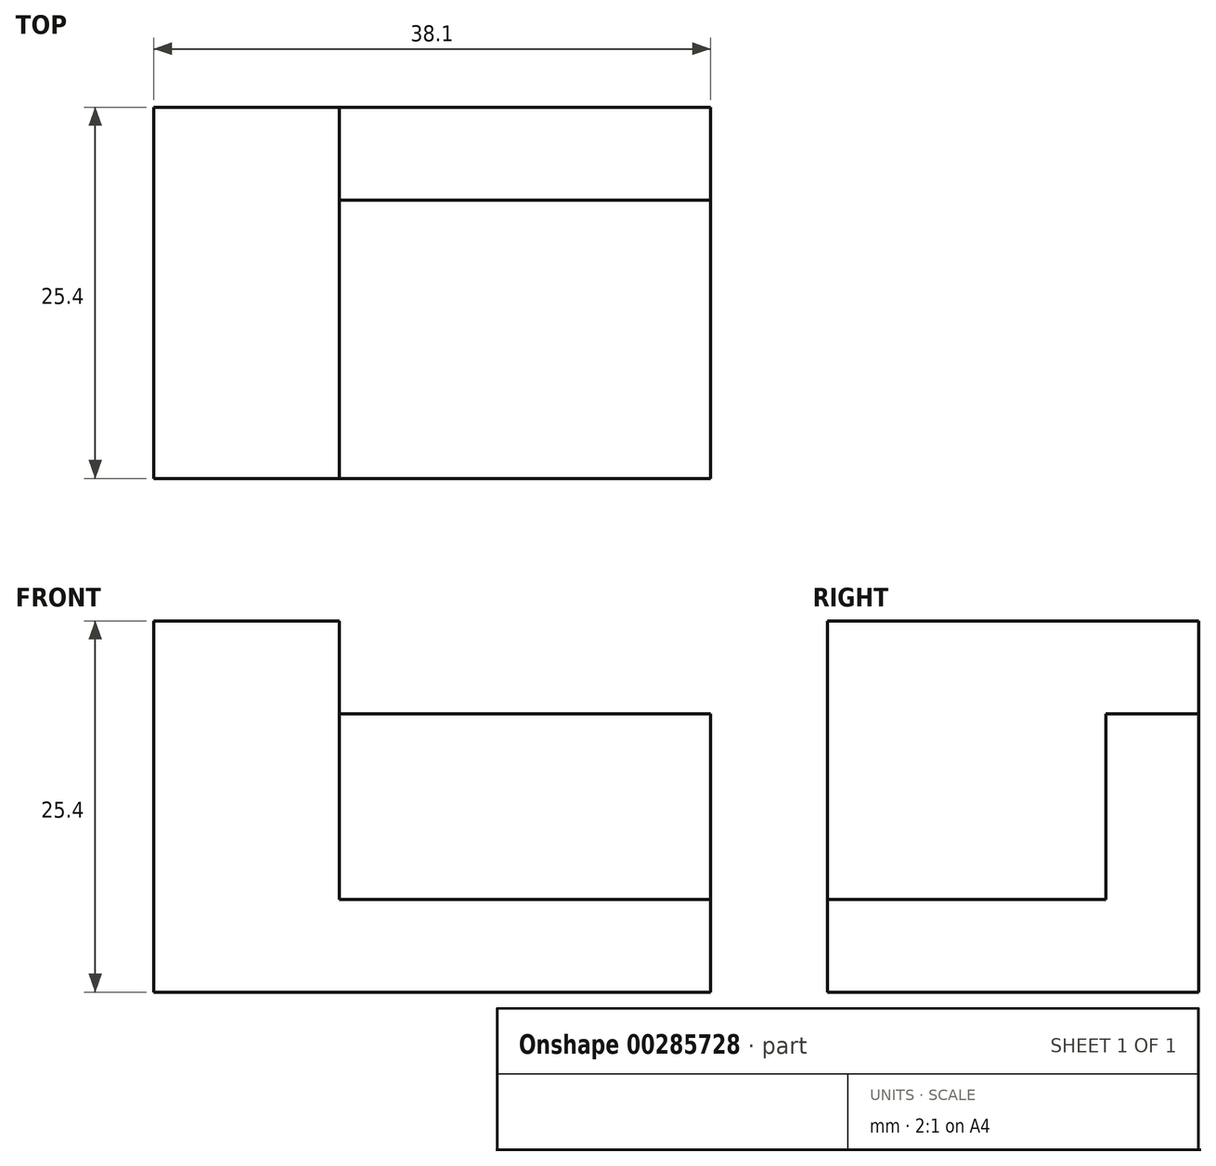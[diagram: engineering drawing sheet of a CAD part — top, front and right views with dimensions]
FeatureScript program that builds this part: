
annotation { "Feature Type Name" : "Feature", "Feature Type Description" : "" }
export const myFeature = defineFeature(function(context is Context, id is Id, definition is map)
    precondition{}
    {
        {
            var Q0;
            Q0=qCreatedBy(makeId("Right.planeOp"),FACE);
            var sketch = newSketch(context, id + "F0", { "sketchPlane" : qUnion([Q0])});
            skLineSegment(sketch, "E0.bottom", {"start": v(0, 25.4) * mm, "end": v(25.4, 25.4) * mm});
            skLineSegment(sketch, "E0.top", {"start": v(0, 0) * mm, "end": v(25.4, 0) * mm});
            skLineSegment(sketch, "E0.left", {"start": v(0, 25.4) * mm, "end": v(0, 0) * mm});
            skLineSegment(sketch, "E0.right", {"start": v(25.4, 25.4) * mm, "end": v(25.4, 0) * mm});
            skSolve(sketch);
        }
        {
            var Q0;
            Q0=makeQuery(id+"F0.imprint","IMPRINT",FACE,{"disambiguationData":[TD([[makeQuery(id+"F0.imprint","IMPRINT",EDGE,{"derivedFrom":sQuery(id+"F0.wireOp",EDGE,"E0.bottom")}),-1.0]])]});
            extrude(context, id + "F1", {"entities" : qUnion([Q0]), "depth" : 38.1 * mm});
        }
        {
            var Q0;
            Q0=makeQuery(id+"F1.opExtrude","CAP_FACE",FACE,{"disambiguationData":[OSD([sQuery(id+"F0.wireOp",EDGE,"E0.bottom"),sQuery(id+"F0.wireOp",EDGE,"E0.top"),sQuery(id+"F0.wireOp",EDGE,"E0.left"),sQuery(id+"F0.wireOp",EDGE,"E0.right")])],"isStart":false});
            var sketch = newSketch(context, id + "F2", { "sketchPlane" : qUnion([Q0])});
            skLineSegment(sketch, "E1", {"start": v(0, 6.35) * mm, "end": v(19.05, 6.35) * mm});
            skLineSegment(sketch, "E2", {"start": v(19.05, 6.35) * mm, "end": v(19.05, 19.05) * mm});
            skLineSegment(sketch, "E3", {"start": v(19.05, 19.05) * mm, "end": v(25.4, 19.05) * mm});
            skLineSegment(sketch, "E4", {"start": v(25.4, 19.05) * mm, "end": v(25.4, 0) * mm});
            skLineSegment(sketch, "E5", {"start": v(25.4, 0) * mm, "end": v(0, 0) * mm});
            skLineSegment(sketch, "E6", {"start": v(0, 0) * mm, "end": v(0, 6.35) * mm});
            skSolve(sketch);
        }
        {
            var Q0;
            {var subQ2=sQuery(id+"F2.wireOp",EDGE,"E1");Q0=makeQuery(id+"F2.imprint","IMPRINT",FACE,{"disambiguationData":[TD([[makeQuery(id+"F2.imprint","IMPRINT",EDGE,{"derivedFrom":subQ2}),1.0]])]});}
            extrude(context, id + "F3", {"entities" : qUnion([Q0]), "operationType" : NewBodyOperationType.REMOVE, "oppositeDirection" : true, "depth" : 25.4 * mm});
        }
    });
